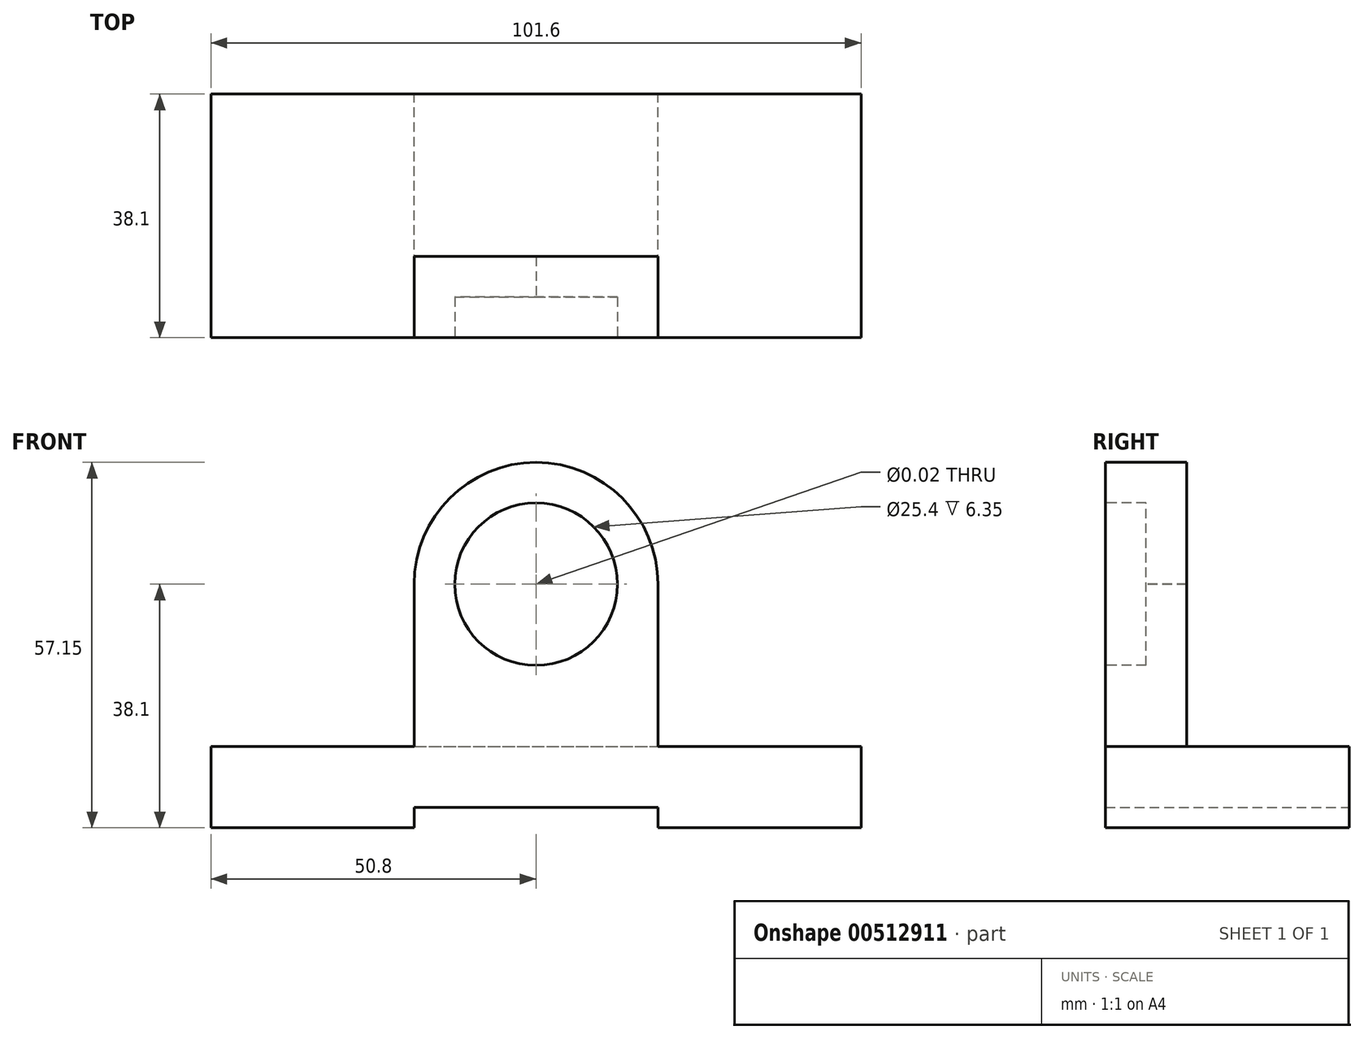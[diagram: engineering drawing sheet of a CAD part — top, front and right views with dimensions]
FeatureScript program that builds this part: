
annotation { "Feature Type Name" : "Feature", "Feature Type Description" : "" }
export const myFeature = defineFeature(function(context is Context, id is Id, definition is map)
    precondition{}
    {
        {
            var Q0;
            Q0=qCreatedBy(makeId("Top.planeOp"),FACE);
            var sketch = newSketch(context, id + "F0", { "sketchPlane" : qUnion([Q0])});
            skLineSegment(sketch, "E0.bottom", {"start": v(0, 0) * mm, "end": v(101.6, 0) * mm});
            skLineSegment(sketch, "E0.top", {"start": v(0, 38.1) * mm, "end": v(101.6, 38.1) * mm});
            skLineSegment(sketch, "E0.left", {"start": v(0, 0) * mm, "end": v(0, 38.1) * mm});
            skLineSegment(sketch, "E0.right", {"start": v(101.6, 0) * mm, "end": v(101.6, 38.1) * mm});
            skSolve(sketch);
        }
        {
            var Q0;
            Q0 = qSketchRegion(id + "F0", true);
            extrude(context, id + "F1", {"entities" : qUnion([Q0]), "depth" : 12.7 * mm});
        }
        {
            var Q0;
            Q0=makeQuery(id+"F1.opExtrude","SWEPT_FACE",FACE,{"disambiguationData":[OSD([sQuery(id+"F0.wireOp",EDGE,"E0.bottom")])]});
            var sketch = newSketch(context, id + "F2", { "sketchPlane" : qUnion([Q0])});
            skLineSegment(sketch, "E1", {"start": v(31.75, 0) * mm, "end": v(31.75, 38.1) * mm});
            skArc(sketch, "E2", {"start": v(69.85, 38.1) * mm, "mid": v(50.8, 57.15) * mm, "end": v(31.75, 38.1) * mm});
            skLineSegment(sketch, "E3", {"start": v(69.85, 38.1) * mm, "end": v(69.85, 0) * mm});
            skLineSegment(sketch, "E4", {"start": v(69.85, 0) * mm, "end": v(31.75, 0) * mm});
            skSolve(sketch);
        }
        {
            var Q0;
            Q0 = qSketchRegion(id + "F2", true);
            extrude(context, id + "F3", {"entities" : qUnion([Q0]), "operationType" : NewBodyOperationType.ADD, "oppositeDirection" : true, "depth" : 12.7 * mm});
        }
        {
            var Q0;
            Q0=sQuery(id+"F2.wireOp",VERTEX,"E2.center");
            var Q1;
            Q1=makeQuery(id+"F1.opExtrude","SWEPT_BODY",BODY,{"disambiguationData":[OSD([sQuery(id+"F0.wireOp",EDGE,"E0.bottom"),sQuery(id+"F0.wireOp",EDGE,"E0.top"),sQuery(id+"F0.wireOp",EDGE,"E0.left"),sQuery(id+"F0.wireOp",EDGE,"E0.right")])]});
            hole(context, id + "F4", {"style" : HoleStyle.C_BORE, "endStyle" : HoleEndStyle.THROUGH, "standardTappedOrClearance" : lookupTablePath({ "standard" : "ANSI", "size" : "15/32 (0.47)", "type" : "Drilled" }), "standardBlindInLast" : lookupTablePath({ "standard" : "ANSI", "size" : "15/32", "type" : "Drilled" }), "holeDiameter" : 15 / 812.8 * mm, "cBoreDiameter" : 25.4 * mm, "cBoreDepth" : 6.35 * mm, "isTappedThrough" : true, "tappedDepth" : 12.7 * mm, "tapClearance" : 3, "locations" : qUnion([Q0]), "scope" : qUnion([Q1])});
        }
        {
            var Q0;
            Q0=makeQuery(id+"F1.opExtrude","SWEPT_FACE",FACE,{"disambiguationData":[OSD([sQuery(id+"F0.wireOp",EDGE,"E0.top")])]});
            var sketch = newSketch(context, id + "F5", { "sketchPlane" : qUnion([Q0])});
            skLineSegment(sketch, "E5", {"start": v(-69.85, 0) * mm, "end": v(-69.85, 3.17) * mm});
            skLineSegment(sketch, "E6", {"start": v(-69.85, 3.17) * mm, "end": v(-31.75, 3.17) * mm});
            skLineSegment(sketch, "E7", {"start": v(-31.75, 3.17) * mm, "end": v(-31.75, 0) * mm});
            skLineSegment(sketch, "E8", {"start": v(-31.75, 0) * mm, "end": v(-69.85, 0) * mm});
            skSolve(sketch);
        }
        {
            var Q0;
            Q0=makeQuery(id+"F5.imprint","IMPRINT",FACE,{"disambiguationData":[TD([[makeQuery(id+"F5.imprint","IMPRINT",EDGE,{"derivedFrom":sQuery(id+"F5.wireOp",EDGE,"E5")}),-1.0]])]});
            extrude(context, id + "F6", {"entities" : qUnion([Q0]), "operationType" : NewBodyOperationType.REMOVE, "endBound" : BoundingType.THROUGH_ALL, "oppositeDirection" : true, "depth" : 50.8 * mm});
        }
    });
